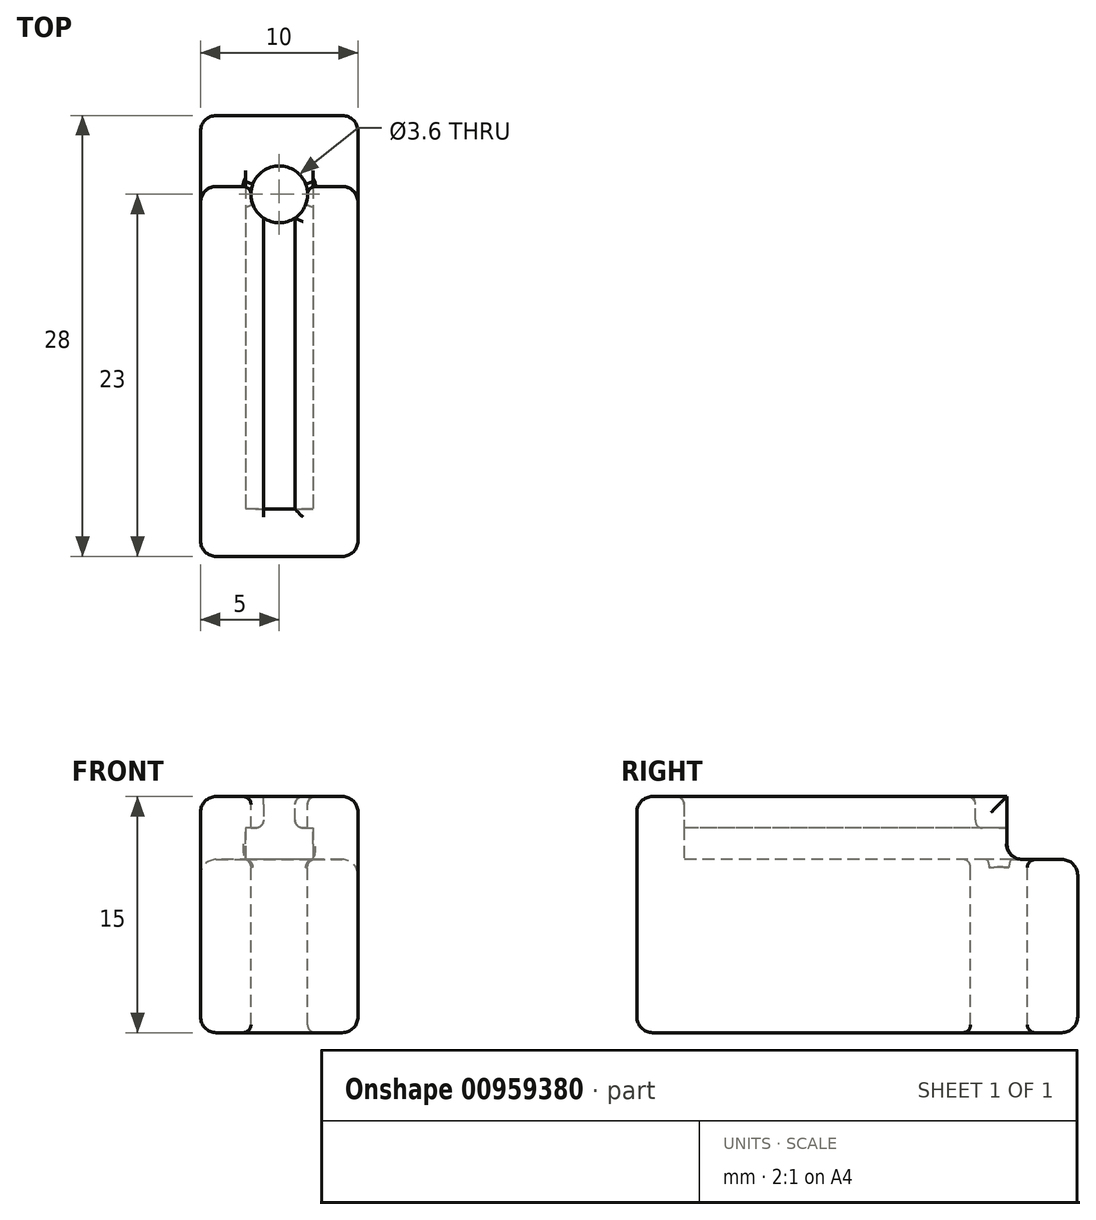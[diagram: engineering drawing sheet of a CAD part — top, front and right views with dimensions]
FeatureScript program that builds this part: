
annotation { "Feature Type Name" : "Feature", "Feature Type Description" : "" }
export const myFeature = defineFeature(function(context is Context, id is Id, definition is map)
    precondition{}
    {
        {
            var Q0;
            Q0=qCreatedBy(makeId("Front.planeOp"),FACE);
            var sketch = newSketch(context, id + "F0", { "sketchPlane" : qUnion([Q0])});
            skLineSegment(sketch, "E0.bottom", {"start": v(0, 0) * mm, "end": v(10, 0) * mm});
            skLineSegment(sketch, "E0.top", {"start": v(0, -15) * mm, "end": v(10, -15) * mm});
            skLineSegment(sketch, "E0.left", {"start": v(0, 0) * mm, "end": v(0, -15) * mm});
            skLineSegment(sketch, "E0.right", {"start": v(10, 0) * mm, "end": v(10, -15) * mm});
            skSolve(sketch);
        }
        {
            var Q0;
            Q0 = qSketchRegion(id + "F0", true);
            extrude(context, id + "F1", {"entities" : qUnion([Q0]), "depth" : 25 * mm, "offsetDistance" : 25 * mm});
        }
        {
            var Q0;
            Q0=makeQuery(id+"F1.opExtrude","CAP_FACE",FACE,{"disambiguationData":[OSD([sQuery(id+"F0.wireOp",EDGE,"E0.bottom"),sQuery(id+"F0.wireOp",EDGE,"E0.top"),sQuery(id+"F0.wireOp",EDGE,"E0.left"),sQuery(id+"F0.wireOp",EDGE,"E0.right")])],"isStart":false});
            var sketch = newSketch(context, id + "F2", { "sketchPlane" : qUnion([Q0])});
            skLineSegment(sketch, "E1", {"start": v(4, 0) * mm, "end": v(4, -2) * mm});
            skLineSegment(sketch, "E2", {"start": v(4, -2) * mm, "end": v(2.85, -2) * mm});
            skLineSegment(sketch, "E3", {"start": v(2.85, -2) * mm, "end": v(2.85, -4) * mm});
            skLineSegment(sketch, "E4", {"start": v(5, 0) * mm, "end": v(5, -15) * mm, "construction": true});
            skLineSegment(sketch, "E5", {"start": v(4, 0) * mm, "end": v(5, 0) * mm});
            skLineSegment(sketch, "E6", {"start": v(5, -4) * mm, "end": v(2.85, -4) * mm});
            skLineSegment(sketch, "E7.MirrorCS", {"start": v(6, 0) * mm, "end": v(6, -2) * mm});
            skLineSegment(sketch, "E8.MirrorCS", {"start": v(6, -2) * mm, "end": v(7.15, -2) * mm});
            skLineSegment(sketch, "E9.MirrorCS", {"start": v(7.15, -2) * mm, "end": v(7.15, -4) * mm});
            skLineSegment(sketch, "E10.MirrorCS", {"start": v(5, -4) * mm, "end": v(7.15, -4) * mm});
            skSolve(sketch);
        }
        {
            var Q0;
            Q0 = qSketchRegion(id + "F2", true);
            var Q1;
            Q1=makeQuery(id+"F2.imprint","IMPRINT",FACE,{"disambiguationData":[TD([[makeQuery(id+"F2.imprint","IMPRINT",EDGE,{"derivedFrom":sQuery(id+"F2.wireOp",EDGE,"E1")}),1.0]])]});
            extrude(context, id + "F3", {"entities" : qUnion([Q0, Q1]), "operationType" : NewBodyOperationType.REMOVE, "oppositeDirection" : true, "depth" : 42.6 * mm, "offsetDistance" : 25 * mm});
        }
        {
            var Q0;
            Q0=makeQuery(id+"F1.opExtrude","SWEPT_FACE",FACE,{"disambiguationData":[OSD([sQuery(id+"F0.wireOp",EDGE,"E0.right")])]});
            var sketch = newSketch(context, id + "F4", { "sketchPlane" : qUnion([Q0])});
            skLineSegment(sketch, "E11.bottom", {"start": v(0, 0) * mm, "end": v(-4.5, 0) * mm});
            skLineSegment(sketch, "E11.top", {"start": v(0, -4) * mm, "end": v(-4.5, -4) * mm});
            skLineSegment(sketch, "E11.left", {"start": v(0, 0) * mm, "end": v(0, -4) * mm});
            skLineSegment(sketch, "E11.right", {"start": v(-4.5, 0) * mm, "end": v(-4.5, -4) * mm});
            skSolve(sketch);
        }
        {
            var Q0;
            Q0 = qSketchRegion(id + "F4", true);
            extrude(context, id + "F5", {"entities" : qUnion([Q0]), "operationType" : NewBodyOperationType.REMOVE, "oppositeDirection" : true, "depth" : 25 * mm, "offsetDistance" : 25 * mm});
        }
        {
            var Q0;
            Q0=makeQuery(id+"F1.opExtrude","CAP_FACE",FACE,{"disambiguationData":[OSD([sQuery(id+"F0.wireOp",EDGE,"E0.bottom"),sQuery(id+"F0.wireOp",EDGE,"E0.top"),sQuery(id+"F0.wireOp",EDGE,"E0.left"),sQuery(id+"F0.wireOp",EDGE,"E0.right")])],"isStart":false});
            var sketch = newSketch(context, id + "F6", { "sketchPlane" : qUnion([Q0])});
            skLineSegment(sketch, "E12.bottom", {"start": v(0, 0) * mm, "end": v(10, 0) * mm});
            skLineSegment(sketch, "E12.top", {"start": v(0, -15) * mm, "end": v(10, -15) * mm});
            skLineSegment(sketch, "E12.left", {"start": v(0, 0) * mm, "end": v(0, -15) * mm});
            skLineSegment(sketch, "E12.right", {"start": v(10, 0) * mm, "end": v(10, -15) * mm});
            skSolve(sketch);
        }
        {
            var Q0;
            Q0 = qSketchRegion(id + "F6", true);
            extrude(context, id + "F7", {"entities" : qUnion([Q0]), "operationType" : NewBodyOperationType.ADD, "depth" : 3 * mm, "offsetDistance" : 25 * mm});
        }
        {
            var Q0;
            Q0=makeQuery(id+"F5.boolean.opBoolean","MERGE",FACE,{"derivedFrom":[makeQuery(id+"F3.boolean.opBoolean","COPY",FACE,{"derivedFrom":makeQuery(id+"F3.opExtrude","SWEPT_FACE",FACE,{"disambiguationData":[OSD([sQuery(id+"F2.wireOp",EDGE,"E6"),sQuery(id+"F2.wireOp",EDGE,"E10.MirrorCS")])]})})],"fromTools":[makeQuery(id+"F5.opExtrude","SWEPT_FACE",FACE,{"disambiguationData":[OSD([sQuery(id+"F4.wireOp",EDGE,"E11.top")])]})]});
            var sketch = newSketch(context, id + "F8", { "sketchPlane" : qUnion([Q0])});
            skCircle(sketch, "E13", {"center": v(5, -5) * mm, "radius": 1.8 * mm});
            skPoint(sketch, "E13.centerSnap0", {"position": v(5, 0) * mm});
            skSolve(sketch);
        }
        {
            var Q0;
            Q0 = qSketchRegion(id + "F8", true);
            extrude(context, id + "F9", {"entities" : qUnion([Q0]), "operationType" : NewBodyOperationType.REMOVE, "endBound" : BoundingType.SYMMETRIC, "oppositeDirection" : true, "depth" : 25 * mm, "offsetDistance" : 25 * mm});
        }
        {
            var Q0;
            {var subQ0=sQuery(id+"F4.wireOp",EDGE,"E11.top");var subQ1=sQuery(id+"F4.wireOp",EDGE,"E11.right");Q0=makeQuery(id+"F5.boolean.opBoolean","COPY",EDGE,{"disambiguationData":[TD([makeQuery(id+"F1.opExtrude","SWEPT_FACE",FACE,{"disambiguationData":[OSD([sQuery(id+"F0.wireOp",EDGE,"E0.right")])]})])],"derivedFrom":makeQuery(id+"F5.opExtrude","SWEPT_EDGE",EDGE,{"disambiguationData":[OSD([subQ0,subQ1])]})});}
            var Q1;
            {var subQ0=sQuery(id+"F4.wireOp",EDGE,"E11.top");var subQ1=sQuery(id+"F4.wireOp",EDGE,"E11.right");Q1=makeQuery(id+"F5.boolean.opBoolean","COPY",EDGE,{"disambiguationData":[TD([makeQuery(id+"F1.opExtrude","SWEPT_FACE",FACE,{"disambiguationData":[OSD([sQuery(id+"F0.wireOp",EDGE,"E0.left")])]})])],"derivedFrom":makeQuery(id+"F5.opExtrude","SWEPT_EDGE",EDGE,{"disambiguationData":[OSD([subQ0,subQ1])]})});}
            var Q2;
            {var subQ0=sQuery(id+"F0.wireOp",EDGE,"E0.right");Q2=makeQuery(id+"F5.boolean.opBoolean","MERGE",EDGE,{"derivedFrom":[makeQuery(id+"F3.boolean.opBoolean","INTERSECT",EDGE,{"derivedFrom":[makeQuery(id+"F1.opExtrude","CAP_FACE",FACE,{"disambiguationData":[OSD([sQuery(id+"F0.wireOp",EDGE,"E0.bottom"),sQuery(id+"F0.wireOp",EDGE,"E0.top"),sQuery(id+"F0.wireOp",EDGE,"E0.left"),subQ0])],"isStart":true}),makeQuery(id+"F3.opExtrude","SWEPT_FACE",FACE,{"disambiguationData":[OSD([sQuery(id+"F2.wireOp",EDGE,"E6"),sQuery(id+"F2.wireOp",EDGE,"E10.MirrorCS")])]})]})],"fromTools":[makeQuery(id+"F5.opExtrude","SWEPT_EDGE",EDGE,{"disambiguationData":[OSD([subQ0,sQuery(id+"F4.wireOp",EDGE,"E11.top"),sQuery(id+"F4.wireOp",EDGE,"E11.left")])]})]});}
            var Q3;
            Q3=makeQuery(id+"F1.opExtrude","CAP_FACE",FACE,{"disambiguationData":[OSD([sQuery(id+"F0.wireOp",EDGE,"E0.bottom"),sQuery(id+"F0.wireOp",EDGE,"E0.top"),sQuery(id+"F0.wireOp",EDGE,"E0.left"),sQuery(id+"F0.wireOp",EDGE,"E0.right")])],"isStart":true});
            var Q4;
            Q4=makeQuery(id+"F7.boolean.opBoolean","MERGE",FACE,{"derivedFrom":[makeQuery(id+"F1.opExtrude","SWEPT_FACE",FACE,{"disambiguationData":[OSD([sQuery(id+"F0.wireOp",EDGE,"E0.right")])]}),makeQuery(id+"F7.opExtrude","SWEPT_FACE",FACE,{"disambiguationData":[OSD([sQuery(id+"F6.wireOp",EDGE,"E12.right")])]})]});
            var Q5;
            Q5=makeQuery(id+"F7.boolean.opBoolean","MERGE",FACE,{"derivedFrom":[makeQuery(id+"F1.opExtrude","SWEPT_FACE",FACE,{"disambiguationData":[OSD([sQuery(id+"F0.wireOp",EDGE,"E0.left")])]}),makeQuery(id+"F7.opExtrude","SWEPT_FACE",FACE,{"disambiguationData":[OSD([sQuery(id+"F6.wireOp",EDGE,"E12.left")])]})]});
            var Q6;
            Q6=makeQuery(id+"F7.opExtrude","CAP_FACE",FACE,{"disambiguationData":[OSD([sQuery(id+"F6.wireOp",EDGE,"E12.bottom"),sQuery(id+"F6.wireOp",EDGE,"E12.top"),sQuery(id+"F6.wireOp",EDGE,"E12.left"),sQuery(id+"F6.wireOp",EDGE,"E12.right")])],"isStart":false});
            fillet(context, id + "F10", {"entities" : qUnion([Q0, Q1, Q2, Q3, Q4, Q5, Q6]), "radius" : 1 * mm, "tangentPropagation" : true, "allowEdgeOverflow" : false});
        }
        {
            var Q0;
            Q0=makeQuery(id+"F3.boolean.opBoolean","COPY",EDGE,{"derivedFrom":makeQuery(id+"F3.opExtrude","SWEPT_EDGE",EDGE,{"disambiguationData":[OSD([sQuery(id+"F0.wireOp",EDGE,"E0.bottom"),sQuery(id+"F2.wireOp",EDGE,"E1"),sQuery(id+"F2.wireOp",EDGE,"E5")])]})});
            var Q1;
            Q1=makeQuery(id+"F7.opExtrude","CAP_EDGE",EDGE,{"disambiguationData":[OSD([sQuery(id+"F6.wireOp",EDGE,"E12.bottom")])],"isStart":true});
            var Q2;
            Q2=makeQuery(id+"F3.boolean.opBoolean","COPY",EDGE,{"derivedFrom":makeQuery(id+"F3.opExtrude","SWEPT_EDGE",EDGE,{"disambiguationData":[OSD([sQuery(id+"F0.wireOp",EDGE,"E0.bottom"),sQuery(id+"F2.wireOp",EDGE,"E7.MirrorCS")])]})});
            var Q3;
            {var subQ0=sQuery(id+"F0.wireOp",EDGE,"E0.right");var subQ1=sQuery(id+"F0.wireOp",EDGE,"E0.left");var subQ3=sQuery(id+"F0.wireOp",EDGE,"E0.bottom");var subQ6=makeQuery(id+"F1.opExtrude","SWEPT_FACE",FACE,{"disambiguationData":[OSD([subQ3])]});Q3=makeQuery(id+"F9.boolean.opBoolean","INTERSECT",EDGE,{"disambiguationData":[OD(1.0)],"derivedFrom":[makeQuery(id+"F7.boolean.opBoolean","MERGE",FACE,{"derivedFrom":[makeQuery(id+"F3.boolean.opBoolean","SPLIT",FACE,{"disambiguationData":[TD([makeQuery(id+"F1.opExtrude","SWEPT_FACE",FACE,{"disambiguationData":[OSD([subQ1])]})])],"derivedFrom":subQ6}),makeQuery(id+"F3.boolean.opBoolean","SPLIT",FACE,{"disambiguationData":[TD([makeQuery(id+"F1.opExtrude","SWEPT_FACE",FACE,{"disambiguationData":[OSD([subQ0])]})])],"derivedFrom":subQ6}),makeQuery(id+"F7.opExtrude","SWEPT_FACE",FACE,{"disambiguationData":[OSD([sQuery(id+"F6.wireOp",EDGE,"E12.bottom")])]})]}),makeQuery(id+"F9.opExtrude","SWEPT_FACE",FACE,{"disambiguationData":[OSD([sQuery(id+"F8.wireOp",EDGE,"E13")])]})]});}
            var Q4;
            {var subQ0=sQuery(id+"F0.wireOp",EDGE,"E0.right");var subQ1=sQuery(id+"F0.wireOp",EDGE,"E0.left");var subQ3=sQuery(id+"F0.wireOp",EDGE,"E0.bottom");var subQ6=makeQuery(id+"F1.opExtrude","SWEPT_FACE",FACE,{"disambiguationData":[OSD([subQ3])]});Q4=makeQuery(id+"F9.boolean.opBoolean","INTERSECT",EDGE,{"disambiguationData":[OD(0.0)],"derivedFrom":[makeQuery(id+"F7.boolean.opBoolean","MERGE",FACE,{"derivedFrom":[makeQuery(id+"F3.boolean.opBoolean","SPLIT",FACE,{"disambiguationData":[TD([makeQuery(id+"F1.opExtrude","SWEPT_FACE",FACE,{"disambiguationData":[OSD([subQ1])]})])],"derivedFrom":subQ6}),makeQuery(id+"F3.boolean.opBoolean","SPLIT",FACE,{"disambiguationData":[TD([makeQuery(id+"F1.opExtrude","SWEPT_FACE",FACE,{"disambiguationData":[OSD([subQ0])]})])],"derivedFrom":subQ6}),makeQuery(id+"F7.opExtrude","SWEPT_FACE",FACE,{"disambiguationData":[OSD([sQuery(id+"F6.wireOp",EDGE,"E12.bottom")])]})]}),makeQuery(id+"F9.opExtrude","SWEPT_FACE",FACE,{"disambiguationData":[OSD([sQuery(id+"F8.wireOp",EDGE,"E13")])]})]});}
            var Q5;
            Q5=makeQuery(id+"F9.boolean.opBoolean","INTERSECT",EDGE,{"derivedFrom":[makeQuery(id+"F5.boolean.opBoolean","COPY",FACE,{"disambiguationData":[TD([makeQuery(id+"F1.opExtrude","SWEPT_FACE",FACE,{"disambiguationData":[OSD([sQuery(id+"F0.wireOp",EDGE,"E0.right")])]})])],"derivedFrom":makeQuery(id+"F5.opExtrude","SWEPT_FACE",FACE,{"disambiguationData":[OSD([sQuery(id+"F4.wireOp",EDGE,"E11.right")])]})}),makeQuery(id+"F9.opExtrude","SWEPT_FACE",FACE,{"disambiguationData":[OSD([sQuery(id+"F8.wireOp",EDGE,"E13")])]})]});
            var Q6;
            Q6=makeQuery(id+"F9.boolean.opBoolean","INTERSECT",EDGE,{"derivedFrom":[makeQuery(id+"F5.boolean.opBoolean","COPY",FACE,{"disambiguationData":[TD([makeQuery(id+"F1.opExtrude","SWEPT_FACE",FACE,{"disambiguationData":[OSD([sQuery(id+"F0.wireOp",EDGE,"E0.left")])]})])],"derivedFrom":makeQuery(id+"F5.opExtrude","SWEPT_FACE",FACE,{"disambiguationData":[OSD([sQuery(id+"F4.wireOp",EDGE,"E11.right")])]})}),makeQuery(id+"F9.opExtrude","SWEPT_FACE",FACE,{"disambiguationData":[OSD([sQuery(id+"F8.wireOp",EDGE,"E13")])]})]});
            var Q7;
            Q7=makeQuery(id+"F3.boolean.opBoolean","COPY",EDGE,{"derivedFrom":makeQuery(id+"F3.opExtrude","SWEPT_EDGE",EDGE,{"disambiguationData":[OSD([sQuery(id+"F2.wireOp",EDGE,"E7.MirrorCS"),sQuery(id+"F2.wireOp",EDGE,"E8.MirrorCS")])]})});
            var Q8;
            Q8=makeQuery(id+"F3.boolean.opBoolean","COPY",EDGE,{"derivedFrom":makeQuery(id+"F3.opExtrude","SWEPT_EDGE",EDGE,{"disambiguationData":[OSD([sQuery(id+"F2.wireOp",EDGE,"E1"),sQuery(id+"F2.wireOp",EDGE,"E2")])]})});
            var Q9;
            Q9=makeQuery(id+"F9.boolean.opBoolean","COPY",FACE,{"disambiguationData":[TD([makeQuery(id+"F1.opExtrude","SWEPT_FACE",FACE,{"disambiguationData":[OSD([sQuery(id+"F0.wireOp",EDGE,"E0.top")])]})])],"derivedFrom":makeQuery(id+"F9.opExtrude","SWEPT_FACE",FACE,{"disambiguationData":[OSD([sQuery(id+"F8.wireOp",EDGE,"E13")])]})});
            fillet(context, id + "F11", {"entities" : qUnion([Q0, Q1, Q2, Q3, Q4, Q5, Q6, Q7, Q8, Q9]), "radius" : 0.5 * mm, "tangentPropagation" : true, "allowEdgeOverflow" : false});
        }
    });
